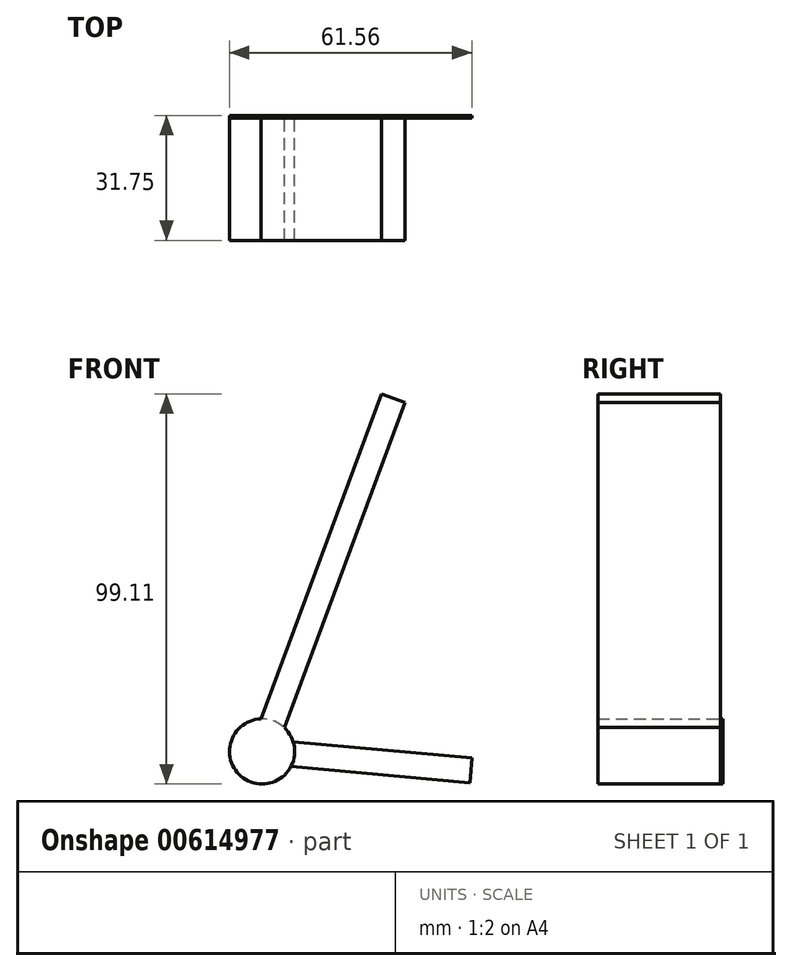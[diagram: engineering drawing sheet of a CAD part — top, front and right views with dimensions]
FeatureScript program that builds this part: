
annotation { "Feature Type Name" : "Feature", "Feature Type Description" : "" }
export const myFeature = defineFeature(function(context is Context, id is Id, definition is map)
    precondition{}
    {
        {
            assignVariable(context, id + "F0", {"name" : "Thickness", "anyValue" : .625});
        }
        {
            var Q0;
            Q0=qCreatedBy(makeId("Front.planeOp"),FACE);
            var sketch = newSketch(context, id + "F1", { "sketchPlane" : qUnion([Q0])});
            skCircle(sketch, "E0", {"center": v(0, 0) * mm, "radius": 8.28 * mm});
            skLineSegment(sketch, "E1", {"start": v(0, 0) * mm, "end": v(33.38, 89.73) * mm, "construction": true});
            skLineSegment(sketch, "E2", {"start": v(-0.31, 8.27) * mm, "end": v(30.4, 90.83) * mm});
            skLineSegment(sketch, "E3", {"start": v(30.4, 90.83) * mm, "end": v(36.36, 88.62) * mm});
            skLineSegment(sketch, "E4", {"start": v(36.36, 88.62) * mm, "end": v(5.64, 6.06) * mm});
            skLineSegment(sketch, "E5", {"start": v(7.9, 2.47) * mm, "end": v(53.28, -1.66) * mm});
            skLineSegment(sketch, "E6", {"start": v(53.28, -1.66) * mm, "end": v(52.83, -8) * mm});
            skLineSegment(sketch, "E7", {"start": v(52.83, -8) * mm, "end": v(7.32, -3.86) * mm});
            skLineSegment(sketch, "E8", {"start": v(0, 0) * mm, "end": v(53.06, -4.83) * mm, "construction": true});
            skSolve(sketch);
        }
        {
            var Q0;
            {var subQ0=sQuery(id+"F1.wireOp",EDGE,"E0");var subQ1=makeQuery(id+"F1.imprint","INTERSECT",VERTEX,{"derivedFrom":[subQ0,sQuery(id+"F1.wireOp",EDGE,"E4")]});Q0=makeQuery(id+"F1.imprint","IMPRINT",FACE,{"disambiguationData":[TD([[makeQuery(id+"F1.imprint","IMPRINT",EDGE,{"disambiguationData":[TD([[subQ1,1.0]])],"derivedFrom":subQ0}),1.0]])]});}
            var Q1;
            {var subQ0=sQuery(id+"F1.wireOp",EDGE,"E2");Q1=makeQuery(id+"F1.imprint","IMPRINT",FACE,{"disambiguationData":[TD([[makeQuery(id+"F1.imprint","IMPRINT",EDGE,{"derivedFrom":subQ0}),-1.0]])]});}
            extrude(context, id + "F2", {"entities" : qUnion([Q0, Q1]), "depth" : (getVariable(context, 'Thickness')) * 50.8 * mm, "offsetDistance" : 25.4 * mm});
        }
        {
            var Q0;
            Q0=makeQuery(id+"F2.opExtrude","CAP_FACE",FACE,{"disambiguationData":[OSD([sQuery(id+"F1.wireOp",EDGE,"E0"),sQuery(id+"F1.wireOp",EDGE,"E2"),sQuery(id+"F1.wireOp",EDGE,"E3"),sQuery(id+"F1.wireOp",EDGE,"E4")])],"isStart":true});
            extrude(context, id + "F3", {"entities" : qUnion([Q0]), "operationType" : NewBodyOperationType.REMOVE, "oppositeDirection" : true, "depth" : (getVariable(context, 'Thickness')) * mm, "offsetDistance" : 25.4 * mm});
        }
        {
            var Q0;
            {var subQ0=sQuery(id+"F1.wireOp",EDGE,"E0");var subQ1=makeQuery(id+"F1.imprint","INTERSECT",VERTEX,{"derivedFrom":[subQ0,sQuery(id+"F1.wireOp",EDGE,"E4")]});Q0=makeQuery(id+"F1.imprint","IMPRINT",FACE,{"disambiguationData":[TD([[makeQuery(id+"F1.imprint","IMPRINT",EDGE,{"disambiguationData":[TD([[subQ1,1.0]])],"derivedFrom":subQ0}),1.0]])]});}
            var Q1;
            {var subQ0=sQuery(id+"F1.wireOp",EDGE,"E5");Q1=makeQuery(id+"F1.imprint","IMPRINT",FACE,{"disambiguationData":[TD([[makeQuery(id+"F1.imprint","IMPRINT",EDGE,{"derivedFrom":subQ0}),-1.0]])]});}
            extrude(context, id + "F4", {"entities" : qUnion([Q0, Q1]), "depth" : (getVariable(context, 'Thickness')) * mm, "offsetDistance" : 25.4 * mm});
        }
    });
